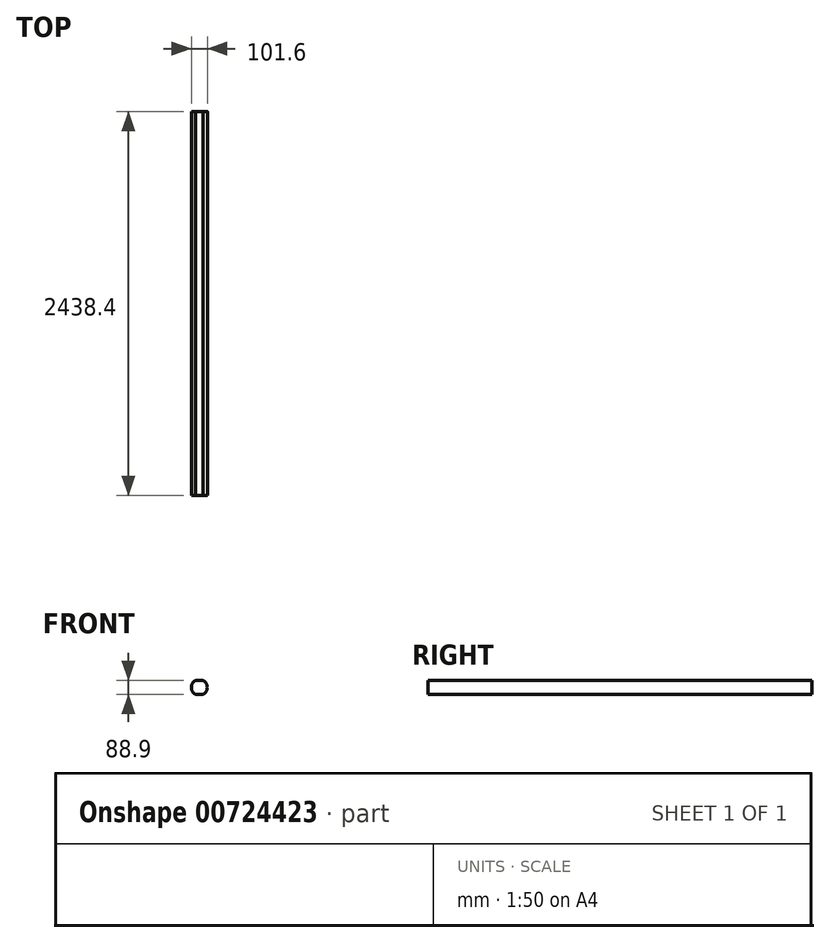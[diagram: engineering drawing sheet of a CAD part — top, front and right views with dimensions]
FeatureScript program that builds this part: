
annotation { "Feature Type Name" : "Feature", "Feature Type Description" : "" }
export const myFeature = defineFeature(function(context is Context, id is Id, definition is map)
    precondition{}
    {
        {
            var Q0;
            Q0=qCreatedBy(makeId("Front.planeOp"),FACE);
            var sketch = newSketch(context, id + "F0", { "sketchPlane" : qUnion([Q0])});
            skArc(sketch, "E0", {"start": v(-24.6, 44.45) * mm, "mid": v(-50.8, 0) * mm, "end": v(-24.6, -44.45) * mm});
            skLineSegment(sketch, "E1.bottom", {"start": v(-24.6, 44.45) * mm, "end": v(24.6, 44.45) * mm});
            skLineSegment(sketch, "E1.top", {"start": v(-24.6, -44.45) * mm, "end": v(24.6, -44.45) * mm});
            skArc(sketch, "E2.trimOffspring", {"start": v(24.6, -44.45) * mm, "mid": v(50.8, 0) * mm, "end": v(24.6, 44.45) * mm});
            skPoint(sketch, "E3.orphan", {"position": v(-44.45, 44.45) * mm});
            skPoint(sketch, "E4.orphan", {"position": v(44.45, 44.45) * mm});
            skPoint(sketch, "E5.orphan", {"position": v(44.45, -44.45) * mm});
            skPoint(sketch, "E6.orphan", {"position": v(-44.45, -44.45) * mm});
            skSolve(sketch);
        }
        {
            var Q0;
            Q0=makeQuery(id+"F0.imprint","IMPRINT",FACE,{"disambiguationData":[TD([[makeQuery(id+"F0.imprint","IMPRINT",EDGE,{"derivedFrom":sQuery(id+"F0.wireOp",EDGE,"E0")}),1.0]])]});
            extrude(context, id + "F1", {"entities" : qUnion([Q0]), "depth" : 2438.4 * mm, "offsetDistance" : 25.4 * mm});
        }
    });
